# Revit family: IS_Oleas_R0121_BIM_DE
name_source: partatom
category: Plumbing Fixtures
revit_build: Autodesk Revit 2017 (Build: 20160225_1515(x64)
units: mm (PartAtom-declared; Revit-internal decimal feet)

## family parameters
Always vertical = No
Cut with Voids When Loaded = No
OmniClass Number = 23.45.00.00
OmniClass Title = Sanitary, Laundry, and Cleaning Equipment
Part Type = Normal
Room Calculation Point = No
Round Connector Dimension = Use Diameter
Shared = No
Work Plane-Based = No

## types (1)
- R0121AA - OLEAS M2 F/PLATE DUAL BLACK - IS
    Accesoires = https://www.idealstandard.de
    Afmetingen = 55 x 265, 245 x 190, 17 mm
    AfstandsEenheid = Millimeter
    Afwerking = Chrome
    Artikelnummer = R0121AA
    Artikelomschrijving = Betätigungsplatte M2 OLEAS. mechanischen Auslösung. Chrom
    Artikelreferentie = Betätigungsplatte M2 OLEAS. mechanischen Auslösung. Chrom
    Assembly Code = C1030200
    Auteur = Ideal Standrad
    BOSUseNativeGeometries = 1
    Barcode = 3391500580329
    Beschrijvinggarantie = Garantie van de fabrikant
    BimObjectNaam = IS_IdealStandard_WCcisternflushpipes_Oleas_R0121
    Breedte = 0
    BrutoGewicht = 0
    CWFU = 0
    Cost = 0 $
    Description = Betätigungsplatte M2 OLEAS. mechanischen Auslösung. Chrom
    Diepte = 0 mm  [stored 0 ft]
    Douchebak = No
    DuurEenheid = Jaren
    Eigenschappen = Betätigungsplatte M2 OLEAS. mechanischen Auslösung. Chrom
    Garantieonderdelen = 5
    Garantieunits = Jaren
    GrootteAfvoergat = 0
    HWFU = 0
    Heefthandvaten = No
    Hoogte = 55
    Hulp = https://www.idealstandard.de
    Installatieinstructies = https://www.idealstandard.de
    Installation instructions = https://www.idealstandard.de
    Kleur = Chrom
    Lengte = 0 mm  [stored 0 ft]
    Manufacturer = https://www.idealstandard.de
    Materiaal = Metall
    Merk = Ideal Standard
    Model = R0121AA
    Montageinstuctie = https://www.idealstandard.de
    Nettogewicht = 0
    Normen = WCcisternflushpipes_Oleas_R0121_IdealStandard
    Overloop = 0 mm  [stored 0 ft]
    Product group = Flushplate
    Productinformatie = https://www.idealstandard.de
    Referentie = R0121AA
    Revisie = 1
    Telefoonnummer = 0049 228 5210
    URL = https://www.idealstandard.de
    Uniclass 2015 Code = Pr_40_20_93_89
    Uniclass 2015 Name = WC cisterns
    Uniclass2015Beschrijving = WC cistern flush pipes
    Uniclass2015Referentie = Pr_40_20_93_90
    Urlproducent = https://www.idealstandard.de
    Versie = 1
    Vervangingskosten = 0
    Verwachtelevensduur = 25
    Volumeunits = liter
    WFU = 0

note: [stored X ft] marks values corroborated as IEEE doubles in the binary element streams (Revit-internal decimal feet)

## geometry (parser evidence)
native form markers: Sweep x2
no freeform markers — native parametric forms only
